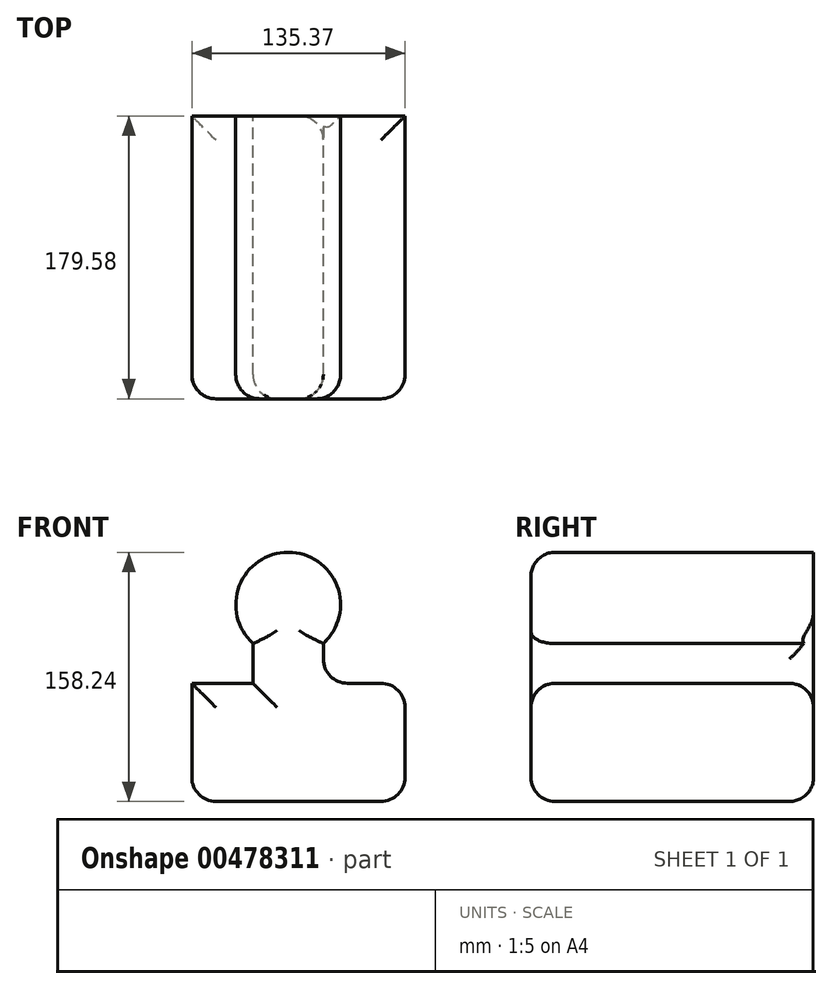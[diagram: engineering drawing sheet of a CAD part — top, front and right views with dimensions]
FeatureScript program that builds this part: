
annotation { "Feature Type Name" : "Feature", "Feature Type Description" : "" }
export const myFeature = defineFeature(function(context is Context, id is Id, definition is map)
    precondition{}
    {
        {
            var Q0;
            Q0=qCreatedBy(makeId("Front.planeOp"),FACE);
            var sketch = newSketch(context, id + "F0", { "sketchPlane" : qUnion([Q0])});
            skLineSegment(sketch, "E0.bottom", {"start": v(-99, 41.08) * mm, "end": v(-60.13, 41.08) * mm});
            skLineSegment(sketch, "E0.top", {"start": v(-99, -33.97) * mm, "end": v(36.36, -33.97) * mm});
            skLineSegment(sketch, "E0.left", {"start": v(-99, 41.08) * mm, "end": v(-99, -33.97) * mm});
            skLineSegment(sketch, "E0.right", {"start": v(36.36, 41.08) * mm, "end": v(36.36, -33.97) * mm});
            skLineSegment(sketch, "E1.left", {"start": v(-60.13, 66.35) * mm, "end": v(-60.13, 41.08) * mm});
            skLineSegment(sketch, "E1.right", {"start": v(-15.48, 66.35) * mm, "end": v(-15.48, 41.08) * mm});
            skLineSegment(sketch, "E2.trimOffspring", {"start": v(-15.48, 41.08) * mm, "end": v(36.36, 41.08) * mm});
            skArc(sketch, "E3", {"start": v(-15.48, 66.35) * mm, "mid": v(-37.8, 124.27) * mm, "end": v(-60.13, 66.35) * mm});
            skSolve(sketch);
        }
        {
            var Q0;
            Q0=makeQuery(id+"F0.imprint","IMPRINT",FACE,{"disambiguationData":[TD([[makeQuery(id+"F0.imprint","IMPRINT",EDGE,{"derivedFrom":sQuery(id+"F0.wireOp",EDGE,"E0.bottom")}),-1.0]])]});
            extrude(context, id + "F1", {"entities" : qUnion([Q0]), "depth" : 179.58 * mm});
        }
        {
            var Q0;
            Q0=makeQuery(id+"F1.opExtrude","SWEPT_FACE",FACE,{"disambiguationData":[OSD([sQuery(id+"F0.wireOp",EDGE,"E2.trimOffspring")])]});
            var Q1;
            Q1=makeQuery(id+"F1.opExtrude","SWEPT_FACE",FACE,{"disambiguationData":[OSD([sQuery(id+"F0.wireOp",EDGE,"E0.top")])]});
            var Q2;
            Q2=makeQuery(id+"F1.opExtrude","CAP_FACE",FACE,{"disambiguationData":[OSD([sQuery(id+"F0.wireOp",EDGE,"E0.bottom"),sQuery(id+"F0.wireOp",EDGE,"E0.top"),sQuery(id+"F0.wireOp",EDGE,"E0.left"),sQuery(id+"F0.wireOp",EDGE,"E0.right"),sQuery(id+"F0.wireOp",EDGE,"E1.left"),sQuery(id+"F0.wireOp",EDGE,"E1.right"),sQuery(id+"F0.wireOp",EDGE,"E2.trimOffspring"),sQuery(id+"F0.wireOp",EDGE,"E3")])],"isStart":false});
            fillet(context, id + "F2", {"entities" : qUnion([Q0, Q1, Q2]), "radius" : 15.33 * mm, "tangentPropagation" : true, "allowEdgeOverflow" : false});
        }
    });
